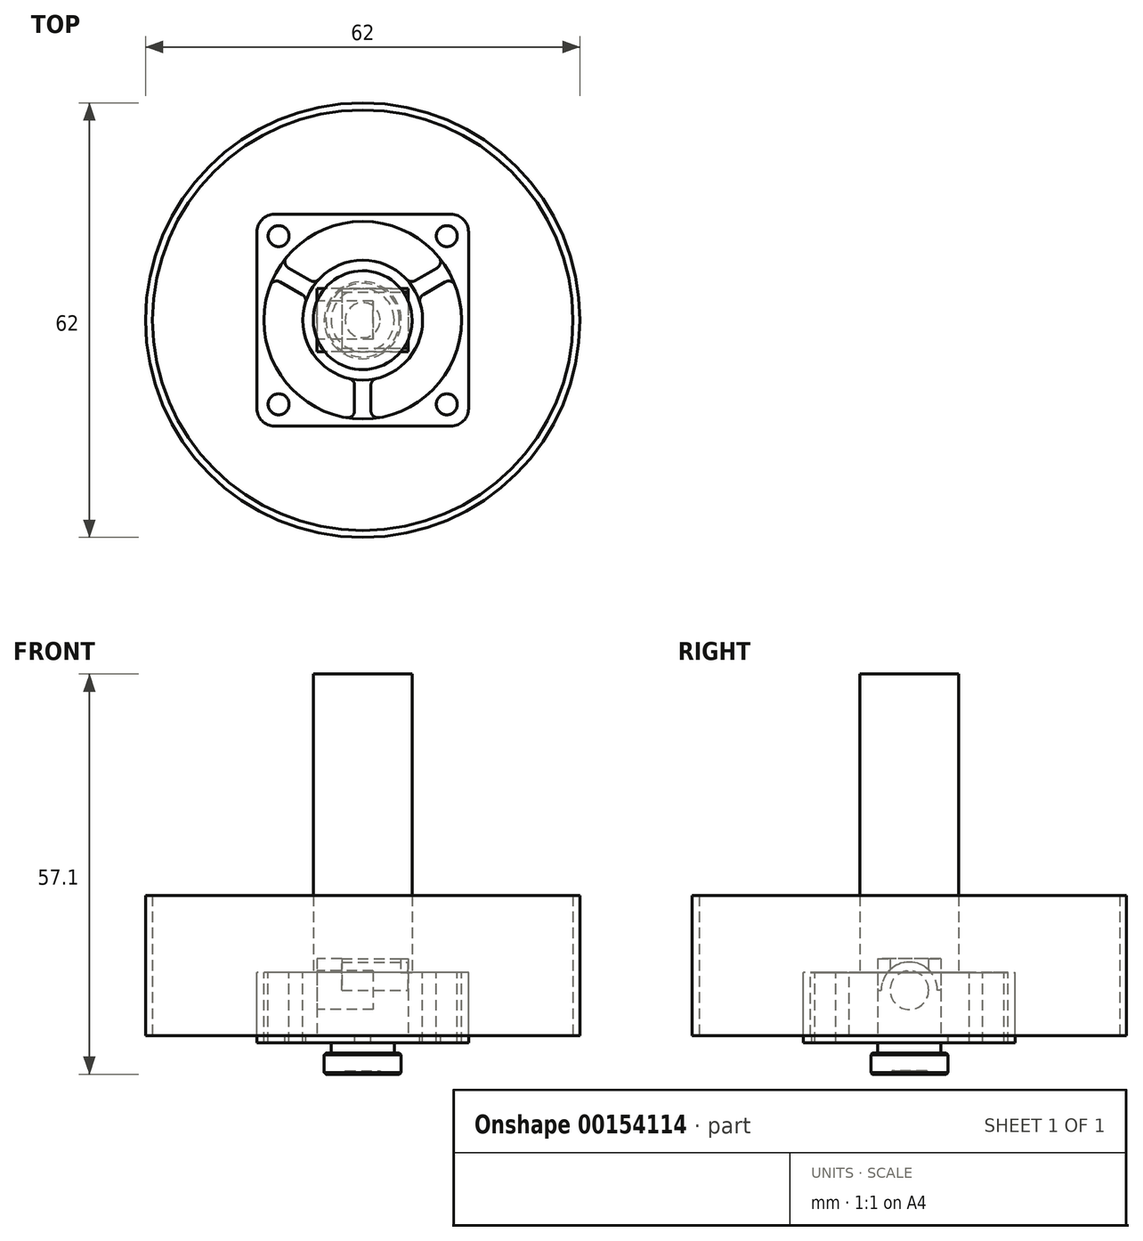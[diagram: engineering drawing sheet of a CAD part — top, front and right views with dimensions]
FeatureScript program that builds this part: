
annotation { "Feature Type Name" : "Feature", "Feature Type Description" : "" }
export const myFeature = defineFeature(function(context is Context, id is Id, definition is map)
    precondition{}
    {
        {
            var Q0;
            Q0=qCreatedBy(makeId("Top.planeOp"),FACE);
            var sketch = newSketch(context, id + "F0", { "sketchPlane" : qUnion([Q0])});
            skCircle(sketch, "E0", {"center": v(0, 0) * mm, "radius": 14.1 * mm});
            skLineSegment(sketch, "E1.bottom", {"start": v(12.6, -15.1) * mm, "end": v(-12.6, -15.1) * mm});
            skLineSegment(sketch, "E1.top", {"start": v(12.6, 15.1) * mm, "end": v(-12.6, 15.1) * mm});
            skLineSegment(sketch, "E1.left", {"start": v(15.1, -12.6) * mm, "end": v(15.1, 12.6) * mm});
            skLineSegment(sketch, "E1.right", {"start": v(-15.1, -12.6) * mm, "end": v(-15.1, 12.6) * mm});
            skCircle(sketch, "E2", {"center": v(12, -12) * mm, "radius": 1.5 * mm});
            skCircle(sketch, "E3.MirrorC", {"center": v(12, 12) * mm, "radius": 1.5 * mm});
            skCircle(sketch, "E4.MirrorC", {"center": v(-12, 12) * mm, "radius": 1.5 * mm});
            skCircle(sketch, "E5.MirrorC", {"center": v(-12, -12) * mm, "radius": 1.5 * mm});
            skCircle(sketch, "E6", {"center": v(0, 0) * mm, "radius": 8.55 * mm});
            skPoint(sketch, "E7.visualSharp", {"position": v(-15.1, 15.1) * mm});
            skArc(sketch, "E7.filletArc", {"start": v(-12.6, 15.1) * mm, "mid": v(-14.37, 14.37) * mm, "end": v(-15.1, 12.6) * mm});
            skPoint(sketch, "E8.visualSharp", {"position": v(15.1, 15.1) * mm});
            skArc(sketch, "E8.filletArc", {"start": v(15.1, 12.6) * mm, "mid": v(14.37, 14.37) * mm, "end": v(12.6, 15.1) * mm});
            skPoint(sketch, "E9.visualSharp", {"position": v(15.1, -15.1) * mm});
            skArc(sketch, "E9.filletArc", {"start": v(12.6, -15.1) * mm, "mid": v(14.37, -14.37) * mm, "end": v(15.1, -12.6) * mm});
            skPoint(sketch, "E10.visualSharp", {"position": v(-15.1, -15.1) * mm});
            skArc(sketch, "E10.filletArc", {"start": v(-15.1, -12.6) * mm, "mid": v(-14.37, -14.37) * mm, "end": v(-12.6, -15.1) * mm});
            skLineSegment(sketch, "E11", {"start": v(0, -8.55) * mm, "end": v(0, -14.1) * mm, "construction": true});
            skPoint(sketch, "E11.endSnap0", {"position": v(0, -15.1) * mm});
            skLineSegment(sketch, "E12.bottom", {"start": v(1.16, -14.87) * mm, "end": v(-1.17, -14.87) * mm, "construction": true});
            skLineSegment(sketch, "E12.top", {"start": v(1.16, -7.78) * mm, "end": v(-1.17, -7.78) * mm, "construction": true});
            skLineSegment(sketch, "E12.left", {"start": v(1.16, -14.87) * mm, "end": v(1.16, -7.78) * mm, "construction": true});
            skLineSegment(sketch, "E12.right", {"start": v(-1.17, -14.87) * mm, "end": v(-1.17, -7.78) * mm, "construction": true});
            skPoint(sketch, "E12.middle", {"position": v(0, -11.32) * mm});
            skLineSegment(sketch, "E13", {"start": v(-1.17, -8.47) * mm, "end": v(-1.17, -14.05) * mm});
            skLineSegment(sketch, "E14", {"start": v(1.16, -8.47) * mm, "end": v(1.16, -14.05) * mm});
            skLineSegment(sketch, "E15.1.0", {"start": v(6.15, 4.9) * mm, "end": v(7.32, 2.88) * mm, "construction": true});
            skLineSegment(sketch, "E15.1.1", {"start": v(13.46, 6.43) * mm, "end": v(7.32, 2.88) * mm, "construction": true});
            skPoint(sketch, "E15.1.2", {"position": v(9.8, 5.66) * mm});
            skPoint(sketch, "E15.1.3", {"position": v(13.08, 7.55) * mm});
            skLineSegment(sketch, "E15.1.4", {"start": v(7.4, 4.27) * mm, "end": v(12.21, 7.05) * mm, "construction": true});
            skLineSegment(sketch, "E15.1.5", {"start": v(12.3, 8.45) * mm, "end": v(6.15, 4.9) * mm, "construction": true});
            skLineSegment(sketch, "E15.1.6", {"start": v(6.75, 5.24) * mm, "end": v(11.59, 8.03) * mm});
            skLineSegment(sketch, "E15.1.7", {"start": v(12.3, 8.45) * mm, "end": v(13.46, 6.43) * mm, "construction": true});
            skLineSegment(sketch, "E15.1.8", {"start": v(7.92, 3.23) * mm, "end": v(12.75, 6.02) * mm});
            skLineSegment(sketch, "E15.2.0", {"start": v(-7.32, 2.88) * mm, "end": v(-6.15, 4.9) * mm, "construction": true});
            skLineSegment(sketch, "E15.2.1", {"start": v(-12.3, 8.45) * mm, "end": v(-6.15, 4.9) * mm, "construction": true});
            skPoint(sketch, "E15.2.2", {"position": v(-9.8, 5.66) * mm});
            skPoint(sketch, "E15.2.3", {"position": v(-13.08, 7.55) * mm});
            skLineSegment(sketch, "E15.2.4", {"start": v(-7.4, 4.28) * mm, "end": v(-12.21, 7.05) * mm, "construction": true});
            skLineSegment(sketch, "E15.2.5", {"start": v(-13.46, 6.43) * mm, "end": v(-7.32, 2.88) * mm, "construction": true});
            skLineSegment(sketch, "E15.2.6", {"start": v(-7.92, 3.23) * mm, "end": v(-12.75, 6.02) * mm});
            skLineSegment(sketch, "E15.2.7", {"start": v(-13.46, 6.43) * mm, "end": v(-12.3, 8.45) * mm, "construction": true});
            skLineSegment(sketch, "E15.2.8", {"start": v(-6.75, 5.24) * mm, "end": v(-11.59, 8.03) * mm});
            skSolve(sketch);
        }
        {
            var Q0;
            Q0=makeQuery(id+"F0.imprint","IMPRINT",FACE,{"disambiguationData":[TD([[makeQuery(id+"F0.imprint","IMPRINT",EDGE,{"derivedFrom":sQuery(id+"F0.wireOp",EDGE,"E0")}),-1.0]])]});
            var Q1;
            {var subQ0=sQuery(id+"F0.wireOp",EDGE,"E13");Q1=makeQuery(id+"F0.imprint","IMPRINT",FACE,{"disambiguationData":[TD([[makeQuery(id+"F0.imprint","IMPRINT",EDGE,{"derivedFrom":subQ0}),1.0]])]});}
            var Q2;
            {var subQ0=sQuery(id+"F0.wireOp",EDGE,"E6");var subQ1=makeQuery(id+"F0.imprint","INTERSECT",VERTEX,{"derivedFrom":[subQ0,sQuery(id+"F0.wireOp",EDGE,"E13")]});Q2=makeQuery(id+"F0.imprint","IMPRINT",FACE,{"disambiguationData":[TD([[makeQuery(id+"F0.imprint","IMPRINT",EDGE,{"disambiguationData":[TD([[subQ1,-1.0]])],"derivedFrom":subQ0}),1.0]])]});}
            var Q3;
            {var subQ0=sQuery(id+"F0.wireOp",EDGE,"E15.2.6");Q3=makeQuery(id+"F0.imprint","IMPRINT",FACE,{"disambiguationData":[TD([[makeQuery(id+"F0.imprint","IMPRINT",EDGE,{"derivedFrom":subQ0}),-1.0]])]});}
            var Q4;
            {var subQ0=sQuery(id+"F0.wireOp",EDGE,"E15.1.6");Q4=makeQuery(id+"F0.imprint","IMPRINT",FACE,{"disambiguationData":[TD([[makeQuery(id+"F0.imprint","IMPRINT",EDGE,{"derivedFrom":subQ0}),-1.0]])]});}
            extrude(context, id + "F1", {"entities" : qUnion([Q0, Q1, Q2, Q3, Q4]), "oppositeDirection" : true, "depth" : 1 * mm});
        }
        {
            var Q0;
            {var subQ0=sQuery(id+"F0.wireOp",EDGE,"E6");var subQ4=makeQuery(id+"F0.imprint","INTERSECT",VERTEX,{"derivedFrom":[subQ0,sQuery(id+"F0.wireOp",EDGE,"E15.1.6")]});Q0=makeQuery(id+"F0.imprint","IMPRINT",FACE,{"disambiguationData":[TD([[makeQuery(id+"F0.imprint","IMPRINT",EDGE,{"disambiguationData":[TD([[subQ4,1.0]])],"derivedFrom":subQ0}),1.0]])]});}
            var Q1;
            Q1=makeQuery(id+"F0.imprint","IMPRINT",FACE,{"disambiguationData":[TD([[makeQuery(id+"F0.imprint","IMPRINT",EDGE,{"derivedFrom":sQuery(id+"F0.wireOp",EDGE,"E1.bottom")}),-1.0]])]});
            extrude(context, id + "F2", {"entities" : qUnion([Q0, Q1]), "operationType" : NewBodyOperationType.ADD, "depth" : 9 * mm});
        }
        {
            var Q0;
            Q0=makeQuery(id+"F1.opExtrude","SWEPT_EDGE",EDGE,{"disambiguationData":[OSD([sQuery(id+"F0.wireOp",EDGE,"E6"),sQuery(id+"F0.wireOp",EDGE,"E15.2.6")])]});
            var Q1;
            Q1=makeQuery(id+"F1.opExtrude","SWEPT_EDGE",EDGE,{"disambiguationData":[OSD([sQuery(id+"F0.wireOp",EDGE,"E6"),sQuery(id+"F0.wireOp",EDGE,"E15.2.8")])]});
            var Q2;
            Q2=makeQuery(id+"F1.opExtrude","SWEPT_EDGE",EDGE,{"disambiguationData":[OSD([sQuery(id+"F0.wireOp",EDGE,"E0"),sQuery(id+"F0.wireOp",EDGE,"E15.2.6")])]});
            var Q3;
            Q3=makeQuery(id+"F1.opExtrude","SWEPT_EDGE",EDGE,{"disambiguationData":[OSD([sQuery(id+"F0.wireOp",EDGE,"E0"),sQuery(id+"F0.wireOp",EDGE,"E15.2.8")])]});
            var Q4;
            Q4=makeQuery(id+"F1.opExtrude","SWEPT_EDGE",EDGE,{"disambiguationData":[OSD([sQuery(id+"F0.wireOp",EDGE,"E0"),sQuery(id+"F0.wireOp",EDGE,"E15.1.6")])]});
            var Q5;
            Q5=makeQuery(id+"F1.opExtrude","SWEPT_EDGE",EDGE,{"disambiguationData":[OSD([sQuery(id+"F0.wireOp",EDGE,"E6"),sQuery(id+"F0.wireOp",EDGE,"E15.1.6")])]});
            var Q6;
            Q6=makeQuery(id+"F1.opExtrude","SWEPT_EDGE",EDGE,{"disambiguationData":[OSD([sQuery(id+"F0.wireOp",EDGE,"E6"),sQuery(id+"F0.wireOp",EDGE,"E15.1.8")])]});
            var Q7;
            Q7=makeQuery(id+"F1.opExtrude","SWEPT_EDGE",EDGE,{"disambiguationData":[OSD([sQuery(id+"F0.wireOp",EDGE,"E0"),sQuery(id+"F0.wireOp",EDGE,"E15.1.8")])]});
            var Q8;
            Q8=makeQuery(id+"F1.opExtrude","SWEPT_EDGE",EDGE,{"disambiguationData":[OSD([sQuery(id+"F0.wireOp",EDGE,"E0"),sQuery(id+"F0.wireOp",EDGE,"E13")])]});
            var Q9;
            Q9=makeQuery(id+"F1.opExtrude","SWEPT_EDGE",EDGE,{"disambiguationData":[OSD([sQuery(id+"F0.wireOp",EDGE,"E0"),sQuery(id+"F0.wireOp",EDGE,"E14")])]});
            var Q10;
            Q10=makeQuery(id+"F1.opExtrude","SWEPT_EDGE",EDGE,{"disambiguationData":[OSD([sQuery(id+"F0.wireOp",EDGE,"E6"),sQuery(id+"F0.wireOp",EDGE,"E13")])]});
            var Q11;
            Q11=makeQuery(id+"F1.opExtrude","SWEPT_EDGE",EDGE,{"disambiguationData":[OSD([sQuery(id+"F0.wireOp",EDGE,"E6"),sQuery(id+"F0.wireOp",EDGE,"E14")])]});
            fillet(context, id + "F3", {"entities" : qUnion([Q0, Q1, Q2, Q3, Q4, Q5, Q6, Q7, Q8, Q9, Q10, Q11]), "radius" : 1 * mm, "tangentPropagation" : true, "allowEdgeOverflow" : false});
        }
        {
            var Q0;
            Q0=qCreatedBy(makeId("Top.planeOp"),FACE);
            var sketch = newSketch(context, id + "F4", { "sketchPlane" : qUnion([Q0])});
            skCircle(sketch, "E16", {"center": v(0, 0) * mm, "radius": 7.05 * mm});
            skCircle(sketch, "E17", {"center": v(0, 0) * mm, "radius": 3.3 * mm});
            skSolve(sketch);
        }
        {
            var Q0;
            Q0=makeQuery(id+"F4.imprint","IMPRINT",FACE,{"disambiguationData":[TD([[makeQuery(id+"F4.imprint","IMPRINT",EDGE,{"derivedFrom":sQuery(id+"F4.wireOp",EDGE,"E16")}),1.0]])]});
            var Q1;
            Q1=makeQuery(id+"F4.imprint","IMPRINT",FACE,{"disambiguationData":[TD([[makeQuery(id+"F4.imprint","IMPRINT",EDGE,{"derivedFrom":sQuery(id+"F4.wireOp",EDGE,"E17")}),1.0]])]});
            extrude(context, id + "F5", {"entities" : qUnion([Q0, Q1]), "depth" : 51.6 * mm});
        }
        {
            var Q0;
            Q0=makeQuery(id+"F4.imprint","IMPRINT",FACE,{"disambiguationData":[TD([[makeQuery(id+"F4.imprint","IMPRINT",EDGE,{"derivedFrom":sQuery(id+"F4.wireOp",EDGE,"E17")}),1.0]])]});
            extrude(context, id + "F6", {"entities" : qUnion([Q0]), "operationType" : NewBodyOperationType.REMOVE, "depth" : 25 * mm});
        }
        {
            var Q0;
            Q0=qCreatedBy(makeId("Top.planeOp"),FACE);
            var sketch = newSketch(context, id + "F7", { "sketchPlane" : qUnion([Q0])});
            skCircle(sketch, "E18", {"center": v(0, 0) * mm, "radius": 7 * mm});
            skCircle(sketch, "E19", {"center": v(0, 0) * mm, "radius": 5.5 * mm});
            skCircle(sketch, "E20", {"center": v(0, 0) * mm, "radius": 4.5 * mm});
            skSolve(sketch);
        }
        {
            var Q0;
            Q0=makeQuery(id+"F7.imprint","IMPRINT",FACE,{"disambiguationData":[TD([[makeQuery(id+"F7.imprint","IMPRINT",EDGE,{"derivedFrom":sQuery(id+"F7.wireOp",EDGE,"E18")}),1.0]])]});
            var Q1;
            Q1=makeQuery(id+"F7.imprint","IMPRINT",FACE,{"disambiguationData":[TD([[makeQuery(id+"F7.imprint","IMPRINT",EDGE,{"derivedFrom":sQuery(id+"F7.wireOp",EDGE,"E20")}),1.0]])]});
            var Q2;
            Q2=makeQuery(id+"F7.imprint","IMPRINT",FACE,{"disambiguationData":[TD([[makeQuery(id+"F7.imprint","IMPRINT",EDGE,{"derivedFrom":sQuery(id+"F7.wireOp",EDGE,"E19")}),1.0]])]});
            extrude(context, id + "F8", {"entities" : qUnion([Q0, Q1, Q2]), "depth" : 37.8 * mm});
        }
        {
            var Q0;
            Q0=makeQuery(id+"F7.imprint","IMPRINT",FACE,{"disambiguationData":[TD([[makeQuery(id+"F7.imprint","IMPRINT",EDGE,{"derivedFrom":sQuery(id+"F7.wireOp",EDGE,"E20")}),1.0]])]});
            extrude(context, id + "F9", {"entities" : qUnion([Q0]), "operationType" : NewBodyOperationType.ADD, "oppositeDirection" : true, "depth" : 2.5 * mm});
        }
        {
            var Q0;
            Q0=makeQuery(id+"F9.opExtrude","CAP_FACE",FACE,{"disambiguationData":[OSD([sQuery(id+"F7.wireOp",EDGE,"E20")])],"isStart":false});
            var sketch = newSketch(context, id + "F10", { "sketchPlane" : qUnion([Q0])});
            skCircle(sketch, "E21", {"center": v(0, 0) * mm, "radius": 5.5 * mm});
            skSolve(sketch);
        }
        {
            var Q0;
            Q0 = qSketchRegion(id + "F10", true);
            extrude(context, id + "F11", {"entities" : qUnion([Q0]), "operationType" : NewBodyOperationType.ADD, "depth" : 3 * mm});
        }
        {
            var Q0;
            Q0=makeQuery(id+"F11.opExtrude","CAP_FACE",FACE,{"disambiguationData":[OSD([sQuery(id+"F10.wireOp",EDGE,"E21")])],"isStart":false});
            var sketch = newSketch(context, id + "F12", { "sketchPlane" : qUnion([Q0])});
            skCircle(sketch, "E22", {"center": v(0, 0) * mm, "radius": 2.5 * mm});
            skSolve(sketch);
        }
        {
            var Q0;
            Q0=makeQuery(id+"F12.imprint","IMPRINT",FACE,{"disambiguationData":[TD([[makeQuery(id+"F12.imprint","IMPRINT",EDGE,{"derivedFrom":sQuery(id+"F12.wireOp",EDGE,"E22")}),1.0]])]});
            extrude(context, id + "F13", {"entities" : qUnion([Q0]), "operationType" : NewBodyOperationType.REMOVE, "oppositeDirection" : true, "depth" : 0.5 * mm});
        }
        {
            var Q0;
            Q0=makeQuery(id+"F11.opExtrude","CAP_EDGE",EDGE,{"disambiguationData":[OSD([sQuery(id+"F10.wireOp",EDGE,"E21")])],"isStart":false});
            var Q1;
            Q1=makeQuery(id+"F11.opExtrude","CAP_EDGE",EDGE,{"disambiguationData":[OSD([sQuery(id+"F10.wireOp",EDGE,"E21")])],"isStart":true});
            var Q2;
            Q2=makeQuery(id+"F8.opExtrude","CAP_EDGE",EDGE,{"disambiguationData":[OSD([sQuery(id+"F7.wireOp",EDGE,"E18")])],"isStart":true});
            var Q3;
            Q3=makeQuery(id+"F8.opExtrude","CAP_EDGE",EDGE,{"disambiguationData":[OSD([sQuery(id+"F7.wireOp",EDGE,"E18")])],"isStart":false});
            var Q4;
            Q4=makeQuery(id+"F13.boolean.opBoolean","COPY",EDGE,{"derivedFrom":makeQuery(id+"F13.opExtrude","CAP_EDGE",EDGE,{"disambiguationData":[OSD([sQuery(id+"F12.wireOp",EDGE,"E22")])],"isStart":true})});
            chamfer(context, id + "F14", {"entities" : qUnion([Q0, Q1, Q2, Q3, Q4]), "width" : 0.25 * mm, "tangentPropagation" : true});
        }
        {
            var Q0;
            Q0=qCreatedBy(makeId("Top.planeOp"),FACE);
            var sketch = newSketch(context, id + "F15", { "sketchPlane" : qUnion([Q0])});
            skCircle(sketch, "E23", {"center": v(0, 0) * mm, "radius": 30 * mm});
            skCircle(sketch, "E24.0", {"center": v(0, 0) * mm, "radius": 31 * mm});
            skSolve(sketch);
        }
        {
            var Q0;
            Q0=makeQuery(id+"F15.imprint","IMPRINT",FACE,{"disambiguationData":[TD([[makeQuery(id+"F15.imprint","IMPRINT",EDGE,{"derivedFrom":sQuery(id+"F15.wireOp",EDGE,"E23")}),-1.0]])]});
            extrude(context, id + "F16", {"entities" : qUnion([Q0]), "depth" : 20 * mm});
        }
        {
            var Q0;
            Q0=qCreatedBy(makeId("Top.planeOp"),FACE);
            var sketch = newSketch(context, id + "F17", { "sketchPlane" : qUnion([Q0])});
            skLineSegment(sketch, "E25.bottom", {"start": v(6.5, 4.5) * mm, "end": v(-6.5, 4.5) * mm});
            skLineSegment(sketch, "E25.top", {"start": v(6.5, -4.5) * mm, "end": v(-6.5, -4.5) * mm});
            skLineSegment(sketch, "E25.left", {"start": v(6.5, 4.5) * mm, "end": v(6.5, -4.5) * mm});
            skLineSegment(sketch, "E25.right", {"start": v(-6.5, 4.5) * mm, "end": v(-6.5, -4.5) * mm});
            skPoint(sketch, "E25.middle", {"position": v(0, 0) * mm});
            skSolve(sketch);
        }
        {
            var Q0;
            Q0=makeQuery(id+"F17.imprint","IMPRINT",FACE,{"disambiguationData":[TD([[makeQuery(id+"F17.imprint","IMPRINT",EDGE,{"derivedFrom":sQuery(id+"F17.wireOp",EDGE,"E25.bottom")}),1.0]])]});
            extrude(context, id + "F18", {"entities" : qUnion([Q0]), "depth" : 11 * mm, "offsetDistance" : 25 * mm});
        }
        {
            var Q0;
            Q0=makeQuery(id+"F18.opExtrude","SWEPT_FACE",FACE,{"disambiguationData":[OSD([sQuery(id+"F17.wireOp",EDGE,"E25.left")])]});
            var sketch = newSketch(context, id + "F19", { "sketchPlane" : qUnion([Q0])});
            skLineSegment(sketch, "E26", {"start": v(-4.5, 6.5) * mm, "end": v(-4, 6.5) * mm});
            skLineSegment(sketch, "E27", {"start": v(4.5, 6.5) * mm, "end": v(4, 6.5) * mm});
            skArc(sketch, "E28", {"start": v(4, 6.5) * mm, "mid": v(0, 10.5) * mm, "end": v(-4, 6.5) * mm});
            skSolve(sketch);
        }
        {
            var Q0;
            {var subQ2=sQuery(id+"F19.wireOp",EDGE,"E28");Q0=makeQuery(id+"F19.imprint","IMPRINT",FACE,{"disambiguationData":[TD([[makeQuery(id+"F19.imprint","IMPRINT",EDGE,{"derivedFrom":subQ2}),-1.0]])]});}
            extrude(context, id + "F20", {"entities" : qUnion([Q0]), "operationType" : NewBodyOperationType.REMOVE, "oppositeDirection" : true, "depth" : 9.5 * mm, "offsetDistance" : 25 * mm});
        }
        {
            var Q0;
            Q0=makeQuery(id+"F18.opExtrude","SWEPT_FACE",FACE,{"disambiguationData":[OSD([sQuery(id+"F17.wireOp",EDGE,"E25.right")])]});
            var sketch = newSketch(context, id + "F21", { "sketchPlane" : qUnion([Q0])});
            skCircle(sketch, "E29", {"center": v(0, 6.5) * mm, "radius": 2.75 * mm});
            skSolve(sketch);
        }
        {
            var Q0;
            Q0 = qSketchRegion(id + "F21", true);
            extrude(context, id + "F22", {"entities" : qUnion([Q0]), "operationType" : NewBodyOperationType.REMOVE, "oppositeDirection" : true, "depth" : 8 * mm, "offsetDistance" : 25 * mm});
        }
    });
